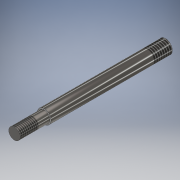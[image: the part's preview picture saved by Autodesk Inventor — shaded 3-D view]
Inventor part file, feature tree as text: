
AUTODESK INVENTOR PART (.ipt)
format: ipt  version: 2017 (Build 210142000, 142)  size: 109,568 bytes
history: native  units: mm
features: extrude x2, thread x2, sketch x2
ambient origin geometry x8: Origin, YZ Plane, XZ Plane, XY Plane, X Axis, Y Axis, Z Axis, Center Point
bodies: Solid1 (feature_tree)
feature tree (6):
  extrude  "Extrusion1"  Depth=13.0mm TaperAngle=0.0deg
  extrude  "Extrusion2"  Depth=53.0mm TaperAngle=0.0deg
  thread  "Thread1"  [1 undecoded]
  thread  "Thread2"  [1 undecoded]
  sketch  "Sketch1"  dims[d0=5.0mm d1=13.0mm d2=0.0mm]
  sketch  "Sketch2"  dims[d3=6.0mm d4=53.0mm d5=0.0mm d6=8.0mm d7=5.0mm d8=8.0mm d9=0.0mm]
note: 2 required parameter values undecoded (feature->parameter linkage not recoverable at this tier; creation-order binding heuristic only, values carry confidence <= 0.55)
